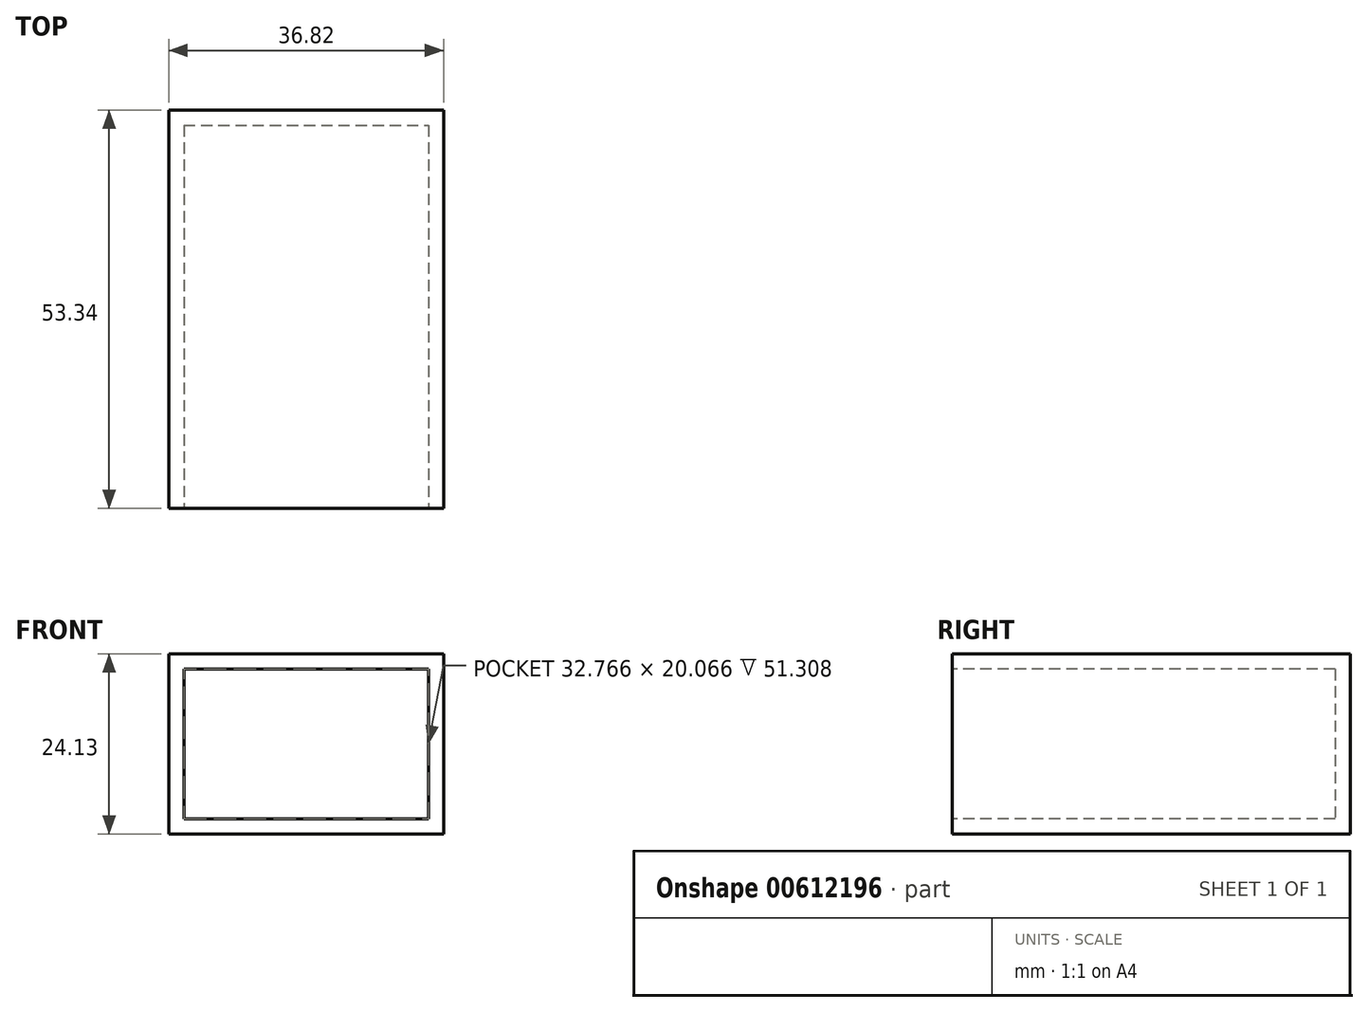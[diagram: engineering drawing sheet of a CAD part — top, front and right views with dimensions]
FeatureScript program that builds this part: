
annotation { "Feature Type Name" : "Feature", "Feature Type Description" : "" }
export const myFeature = defineFeature(function(context is Context, id is Id, definition is map)
    precondition{}
    {
        {
            var Q0;
            Q0=qCreatedBy(makeId("Top.planeOp"),FACE);
            var sketch = newSketch(context, id + "F0", { "sketchPlane" : qUnion([Q0])});
            skLineSegment(sketch, "E0.bottom", {"start": v(-18.41, 26.67) * mm, "end": v(18.42, 26.67) * mm});
            skLineSegment(sketch, "E0.top", {"start": v(-18.42, -26.67) * mm, "end": v(18.41, -26.67) * mm});
            skLineSegment(sketch, "E0.left", {"start": v(-18.41, 26.67) * mm, "end": v(-18.42, -26.67) * mm});
            skLineSegment(sketch, "E0.right", {"start": v(18.42, 26.67) * mm, "end": v(18.41, -26.67) * mm});
            skPoint(sketch, "E0.middle", {"position": v(0, 0) * mm});
            skSolve(sketch);
        }
        {
            var Q0;
            Q0 = qSketchRegion(id + "F0", true);
            extrude(context, id + "F1", {"entities" : qUnion([Q0]), "depth" : 24.13 * mm, "offsetDistance" : 25.4 * mm});
        }
        {
            var Q0;
            Q0=makeQuery(id+"F1.opExtrude","SWEPT_FACE",FACE,{"disambiguationData":[OSD([sQuery(id+"F0.wireOp",EDGE,"E0.top")])]});
            shell(context, id + "F2", {"entities" : qUnion([Q0]), "thickness" : 2.03 * mm});
        }
    });
